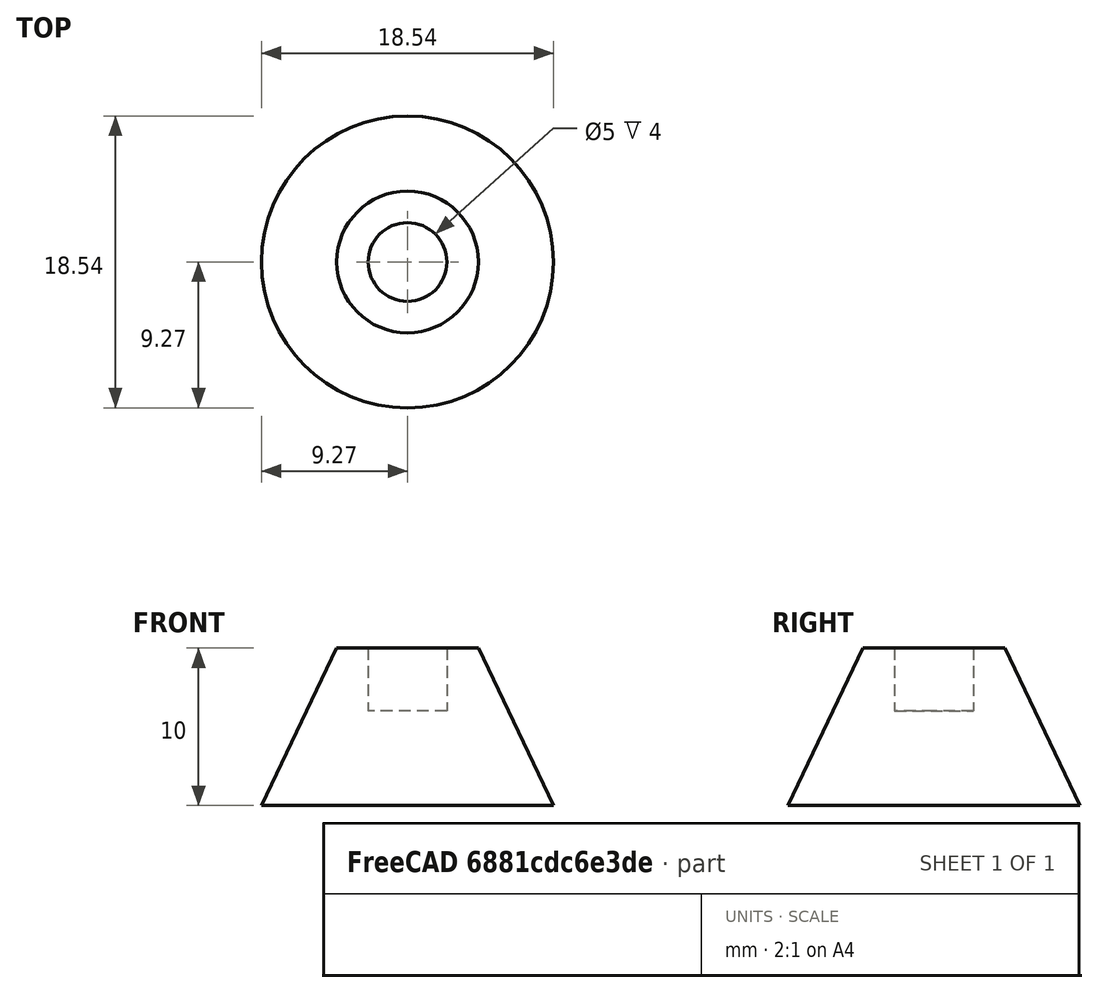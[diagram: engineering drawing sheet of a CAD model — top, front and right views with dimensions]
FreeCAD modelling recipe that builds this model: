
FCSTD DOCUMENT  (FreeCAD 1.0R39109 (Git))
Label: mount_stud
License: All rights reserved
LicenseURL: https://en.wikipedia.org/wiki/All_rights_reserved
objects: Spreadsheet::Sheet×1, Sketcher::SketchObject×1, PartDesign::Revolution×1, PartDesign::Body×1
note: 6 computed .brp shape members not serialized (recipe doc carries the construction recipe); baked Part::Feature solids carry a one-line shape summary decoded from their .brp

FEATURE [Spreadsheet::Sheet] Spreadsheet002  label="MountStudSS"
  Body = 0
  cells = B1='height; C1='base_diameter; D1='top_diameter; E1='barrel_diameter; F1='barrel_depth; G1='depth_padding; H1='horizontal_padding; I1='slope_angle; J1='top_diameter_excluding_barrel; A2==hiddenref(.Body.String); B2(height)==.B3; C2(base_diameter)==.C3; D2(top_diameter)==.D3; E2(barrel_diameter)==.E3; F2(barrel_depth)==.F3; G2(depth_padding)==.G3; H2(horizontal_padding)==.H3; I2(slope_angle)==.I3; J2(top_diameter_excluding_barrel)==.J3; A3='M2 Heated; B3==10 mm; C3==tan(slope_angle) * height * 2 + top_diameter; D3==barrel_diameter + horizontal_padding; E3==5 mm; F3==4 mm; G3==2 mm; H3==2 mm; I3==30 deg; J3==top_diameter - barrel_diameter
  expr: .Body.Enum = cells[<<A3:|>>]
  expr: .cells.Bind.B2.ZZ2 = tuple(.cells; <<B>> + str(hiddenref(Body) + 3); <<ZZ>> + str(hiddenref(Body) + 3))
FEATURE [Sketcher::SketchObject] Sketch
  ArcFitTolerance = 1e-06
  AttachmentSupport = -> [XZ_Plane]
  FullyConstrained = true
  MakeInternals = false
  MapMode = 5
  Placement = pos=(0,0,0) rot=(1,0,0;1.5708rad)
  expr: Constraints[10] = <<MountStudSS>>.barrel_diameter / 2
  expr: Constraints[13] = <<MountStudSS>>.barrel_depth
  expr: Constraints[14] = <<MountStudSS>>.top_diameter_excluding_barrel
  expr: Constraints[15] = <<MountStudSS>>.height
  expr: Constraints[16] = <<MountStudSS>>.base_diameter / 2
  sketch-geometry (6):
    g0: LineSegment StartX=2.5 StartY=10 StartZ=0 EndX=2.5 EndY=6 EndZ=0
    g1: LineSegment StartX=2.5 StartY=6 StartZ=0 EndX=0 EndY=6 EndZ=0
    g2: LineSegment StartX=0 StartY=6 StartZ=0 EndX=0 EndY=0 EndZ=0
    g3: LineSegment StartX=0 StartY=0 StartZ=0 EndX=9.2735 EndY=0 EndZ=0
    g4: LineSegment StartX=9.2735 StartY=0 StartZ=0 EndX=4.5 EndY=10 EndZ=0
    g5: LineSegment StartX=4.5 StartY=10 StartZ=0 EndX=2.5 EndY=10 EndZ=0
  constraints (17):
    c: Vertical(g0)
    c: Coincident(g0,g1)
    c: Coincident(g1,g2)
    c: Coincident(g2,g-1)
    c: Vertical(g2)
    c: Coincident(g2,g3)
    c: PointOnObject(g3,g-1)
    c: Coincident(g3,g4)
    c: Coincident(g4,g5)
    c: Coincident(g5,g0)
    c: Distance(g1) = 2.5
    c: Angle(g0,g1) = 1.5708
    c: Angle(g0,g5) = 1.5708
    c: Distance(g0) = 4
    c: Distance(g5) = 2
    c: DistanceY(g-1,g0) = 10
    c: Distance(g3) = 9.2735
FEATURE [PartDesign::Revolution] Revolution
  Angle = 360
  Angle2 = 60
  Axis = (0,2e-16,1)
  Base = (0,0,0)
  Placement = pos=(0,0,0) rot=(1,0,0;1.5708rad)
  Profile = -> Sketch
  ReferenceAxis = -> Sketch [V_Axis]
  Refine = true
  Reversed = true
  Suppressed = false
  Type = 0
FEATURE [PartDesign::Body] Body  label="MountStud"
  AllowCompound = false
  Group = -> [Sketch,Revolution]
  Origin = -> Origin
  Tip = -> Revolution
